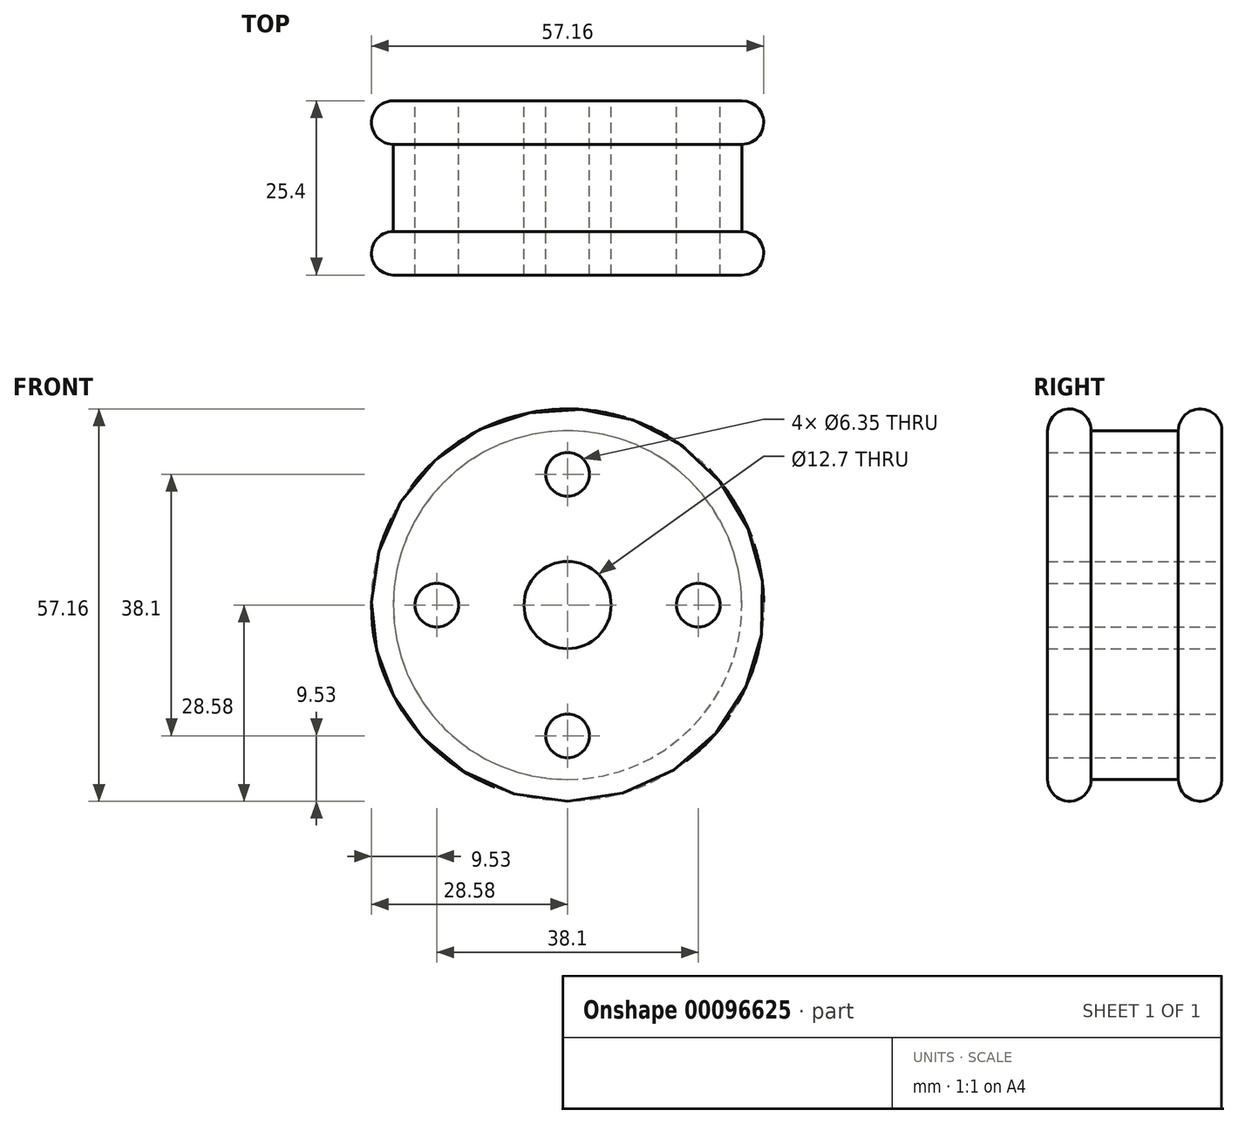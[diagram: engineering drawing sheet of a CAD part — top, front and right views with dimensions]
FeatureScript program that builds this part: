
annotation { "Feature Type Name" : "Feature", "Feature Type Description" : "" }
export const myFeature = defineFeature(function(context is Context, id is Id, definition is map)
    precondition{}
    {
        {
            var Q0;
            Q0=qCreatedBy(makeId("Front.planeOp"),FACE);
            var sketch = newSketch(context, id + "F0", { "sketchPlane" : qUnion([Q0])});
            skCircle(sketch, "E0", {"center": v(0, 0) * mm, "radius": 25.4 * mm});
            skSolve(sketch);
        }
        {
            var Q0;
            Q0 = qSketchRegion(id + "F0", true);
            extrude(context, id + "F1", {"entities" : qUnion([Q0]), "depth" : 12.7 * mm});
        }
        {
            var Q0;
            Q0=makeQuery(id+"F1.opExtrude","CAP_FACE",FACE,{"disambiguationData":[OSD([sQuery(id+"F0.wireOp",EDGE,"E0")])],"isStart":false});
            var sketch = newSketch(context, id + "F2", { "sketchPlane" : qUnion([Q0])});
            skCircle(sketch, "E1", {"center": v(0, 0) * mm, "radius": 28.58 * mm});
            skSolve(sketch);
        }
        {
            var Q0;
            Q0 = qSketchRegion(id + "F2", true);
            extrude(context, id + "F3", {"entities" : qUnion([Q0]), "operationType" : NewBodyOperationType.ADD, "depth" : 6.35 * mm});
        }
        {
            var Q0;
            Q0=makeQuery(id+"F1.opExtrude","CAP_FACE",FACE,{"disambiguationData":[OSD([sQuery(id+"F0.wireOp",EDGE,"E0")])],"isStart":true});
            var sketch = newSketch(context, id + "F4", { "sketchPlane" : qUnion([Q0])});
            skCircle(sketch, "E2.0", {"center": v(0, 0) * mm, "radius": 28.58 * mm});
            skSolve(sketch);
        }
        {
            var Q0;
            Q0 = qSketchRegion(id + "F4", true);
            extrude(context, id + "F5", {"entities" : qUnion([Q0]), "operationType" : NewBodyOperationType.ADD, "depth" : 6.35 * mm});
        }
        {
            var Q0;
            Q0=makeQuery(id+"F5.opExtrude","CAP_FACE",FACE,{"disambiguationData":[OSD([sQuery(id+"F4.wireOp",EDGE,"E2.0")])],"isStart":false});
            var sketch = newSketch(context, id + "F6", { "sketchPlane" : qUnion([Q0])});
            skCircle(sketch, "E3", {"center": v(0, 0) * mm, "radius": 6.35 * mm});
            skSolve(sketch);
        }
        {
            var Q0;
            Q0 = qSketchRegion(id + "F6", true);
            extrude(context, id + "F7", {"entities" : qUnion([Q0]), "operationType" : NewBodyOperationType.REMOVE, "endBound" : BoundingType.THROUGH_ALL, "oppositeDirection" : true, "depth" : 25.4 * mm});
        }
        {
            var Q0;
            Q0=makeQuery(id+"F5.opExtrude","CAP_FACE",FACE,{"disambiguationData":[OSD([sQuery(id+"F4.wireOp",EDGE,"E2.0")])],"isStart":false});
            var sketch = newSketch(context, id + "F8", { "sketchPlane" : qUnion([Q0])});
            skPoint(sketch, "E4", {"position": v(0, 19.05) * mm});
            skPoint(sketch, "E5", {"position": v(19.05, 0) * mm});
            skPoint(sketch, "E6", {"position": v(0, -19.05) * mm});
            skPoint(sketch, "E7", {"position": v(-19.05, 0) * mm});
            skSolve(sketch);
        }
        {
            var Q0;
            Q0=sQuery(id+"F8.wireOp",VERTEX,"E4");
            var Q1;
            Q1=sQuery(id+"F8.wireOp",VERTEX,"E5");
            var Q2;
            Q2=sQuery(id+"F8.wireOp",VERTEX,"E6");
            var Q3;
            Q3=sQuery(id+"F8.wireOp",VERTEX,"E7");
            var Q4;
            Q4=makeQuery(id+"F1.opExtrude","SWEPT_BODY",BODY,{"disambiguationData":[OSD([sQuery(id+"F0.wireOp",EDGE,"E0")])]});
            hole(context, id + "F9", {"style" : HoleStyle.SIMPLE, "endStyle" : HoleEndStyle.THROUGH, "holeDiameter" : 6.35 * mm, "locations" : qUnion([Q0, Q1, Q2, Q3]), "scope" : qUnion([Q4]), "isTappedThrough" : true});
        }
        {
            var Q0;
            Q0=makeQuery(id+"F5.opExtrude","CAP_EDGE",EDGE,{"disambiguationData":[OSD([sQuery(id+"F4.wireOp",EDGE,"E2.0")])],"isStart":false});
            var Q1;
            Q1=makeQuery(id+"F5.opExtrude","CAP_EDGE",EDGE,{"disambiguationData":[OSD([sQuery(id+"F4.wireOp",EDGE,"E2.0")])],"isStart":true});
            var Q2;
            Q2=makeQuery(id+"F3.opExtrude","CAP_EDGE",EDGE,{"disambiguationData":[OSD([sQuery(id+"F2.wireOp",EDGE,"E1")])],"isStart":true});
            var Q3;
            Q3=makeQuery(id+"F3.opExtrude","CAP_EDGE",EDGE,{"disambiguationData":[OSD([sQuery(id+"F2.wireOp",EDGE,"E1")])],"isStart":false});
            fillet(context, id + "F10", {"entities" : qUnion([Q0, Q1, Q2, Q3]), "radius" : 3.17 * mm, "tangentPropagation" : true, "allowEdgeOverflow" : false});
        }
    });
